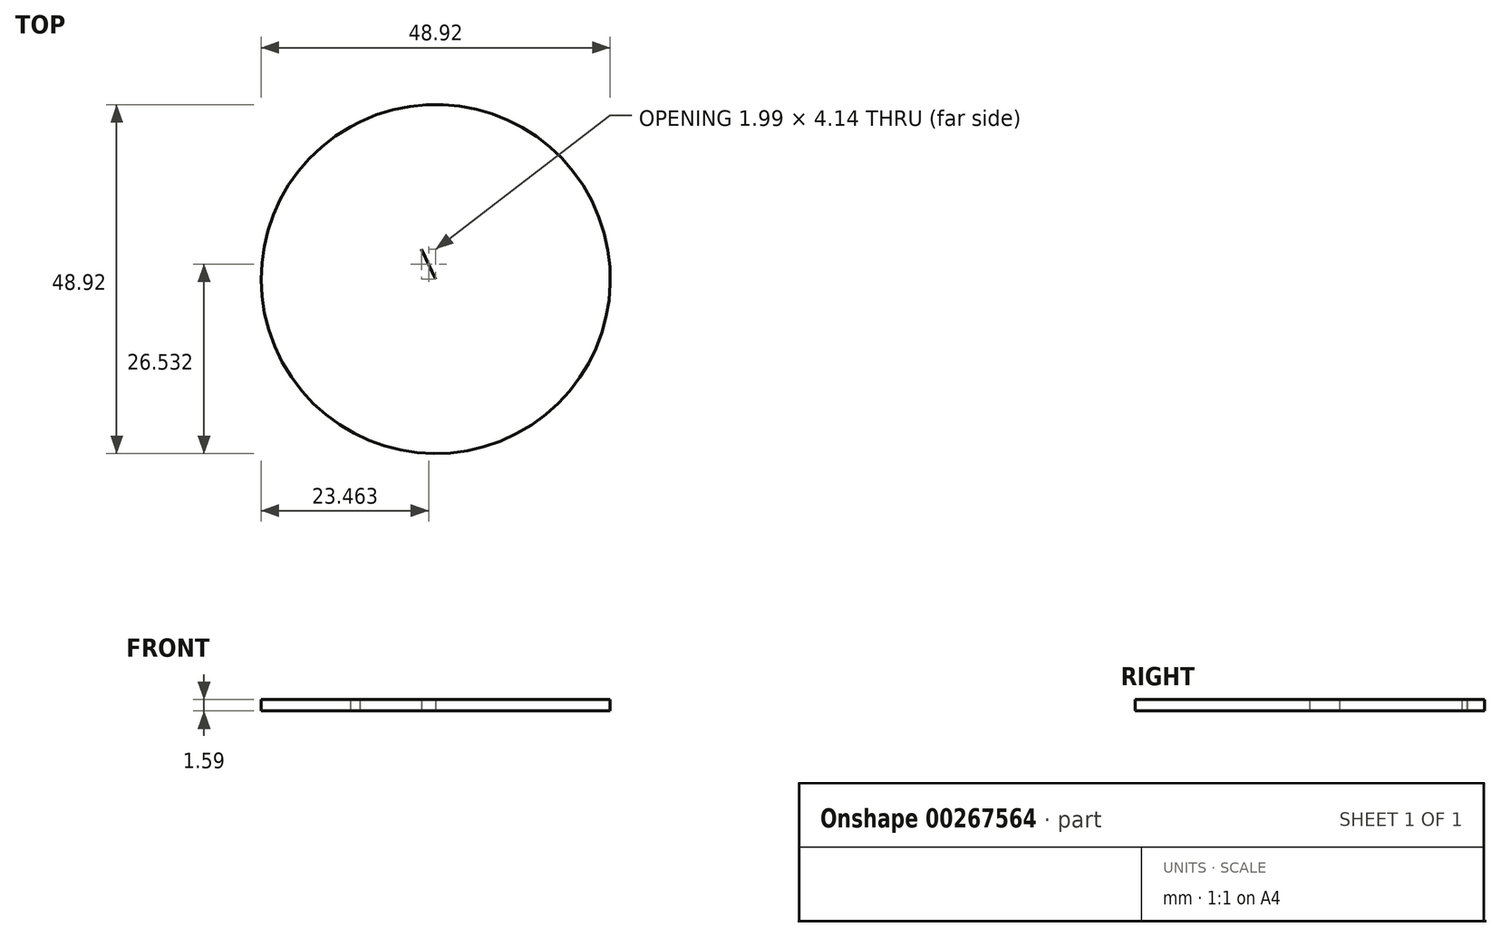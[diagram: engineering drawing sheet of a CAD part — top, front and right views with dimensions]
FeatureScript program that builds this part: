
annotation { "Feature Type Name" : "Feature", "Feature Type Description" : "" }
export const myFeature = defineFeature(function(context is Context, id is Id, definition is map)
    precondition{}
    {
        {
            var Q0;
            Q0=qCreatedBy(makeId("Top.planeOp"),FACE);
            var sketch = newSketch(context, id + "F0", { "sketchPlane" : qUnion([Q0])});
            skCircle(sketch, "E0", {"center": v(0, 0) * mm, "radius": 24.46 * mm});
            skLineSegment(sketch, "E1", {"start": v(-11.97, 21.34) * mm, "end": v(-10.58, 22) * mm});
            skArc(sketch, "E2", {"start": v(-20.14, 0) * mm, "mid": v(8.74, -18.15) * mm, "end": v(12.56, 15.75) * mm});
            skCircle(sketch, "E3", {"center": v(-10.58, 22) * mm, "radius": 1.27 * mm});
            skLineSegment(sketch, "E4", {"start": v(-10.61, 22.04) * mm, "end": v(-10.6, 22) * mm});
            skArc(sketch, "E5.trimOffspring", {"start": v(-8.73, 18.16) * mm, "mid": v(-8.73, 18.15) * mm, "end": v(-8.74, 18.15) * mm});
            skArc(sketch, "E6", {"start": v(-20.14, 0) * mm, "mid": v(-2, 4.14) * mm, "end": v(12.56, 15.75) * mm});
            skLineSegment(sketch, "E7.trimOffspring", {"start": v(-2, 4.14) * mm, "end": v(0, 0) * mm});
            skSolve(sketch);
        }
        {
            var Q0;
            {var subQ2=sQuery(id+"F0.wireOp",EDGE,"E2");Q0=makeQuery(id+"F0.imprint","IMPRINT",FACE,{"disambiguationData":[TD([[makeQuery(id+"F0.imprint","IMPRINT",EDGE,{"derivedFrom":subQ2}),1.0]])]});}
            extrude(context, id + "F1", {"entities" : qUnion([Q0]), "depth" : 1.59 * mm});
        }
        {
            var Q0;
            {var subQ5=sQuery(id+"F0.wireOp",EDGE,"E2");Q0=makeQuery(id+"F0.imprint","IMPRINT",FACE,{"disambiguationData":[TD([[makeQuery(id+"F0.imprint","IMPRINT",EDGE,{"derivedFrom":subQ5}),-1.0]])]});}
            extrude(context, id + "F2", {"entities" : qUnion([Q0]), "depth" : 1.59 * mm});
        }
        {
            var Q0;
            {var subQ5=sQuery(id+"F0.wireOp",EDGE,"E2");Q0=makeQuery(id+"F0.imprint","IMPRINT",FACE,{"disambiguationData":[TD([[makeQuery(id+"F0.imprint","IMPRINT",EDGE,{"derivedFrom":subQ5}),-1.0]])]});}
            var Q1;
            {var subQ2=sQuery(id+"F0.wireOp",EDGE,"E2");Q1=makeQuery(id+"F0.imprint","IMPRINT",FACE,{"disambiguationData":[TD([[makeQuery(id+"F0.imprint","IMPRINT",EDGE,{"derivedFrom":subQ2}),1.0]])]});}
            var Q2;
            {var subQ0=sQuery(id+"F0.wireOp",EDGE,"E4");Q2=makeQuery(id+"F0.imprint","IMPRINT",FACE,{"disambiguationData":[TD([[makeQuery(id+"F0.imprint","IMPRINT",EDGE,{"derivedFrom":subQ0}),1.0]])]});}
            extrude(context, id + "F3", {"entities" : qUnion([Q0, Q1, Q2]), "operationType" : NewBodyOperationType.ADD, "depth" : 1.59 * mm});
        }
    });
